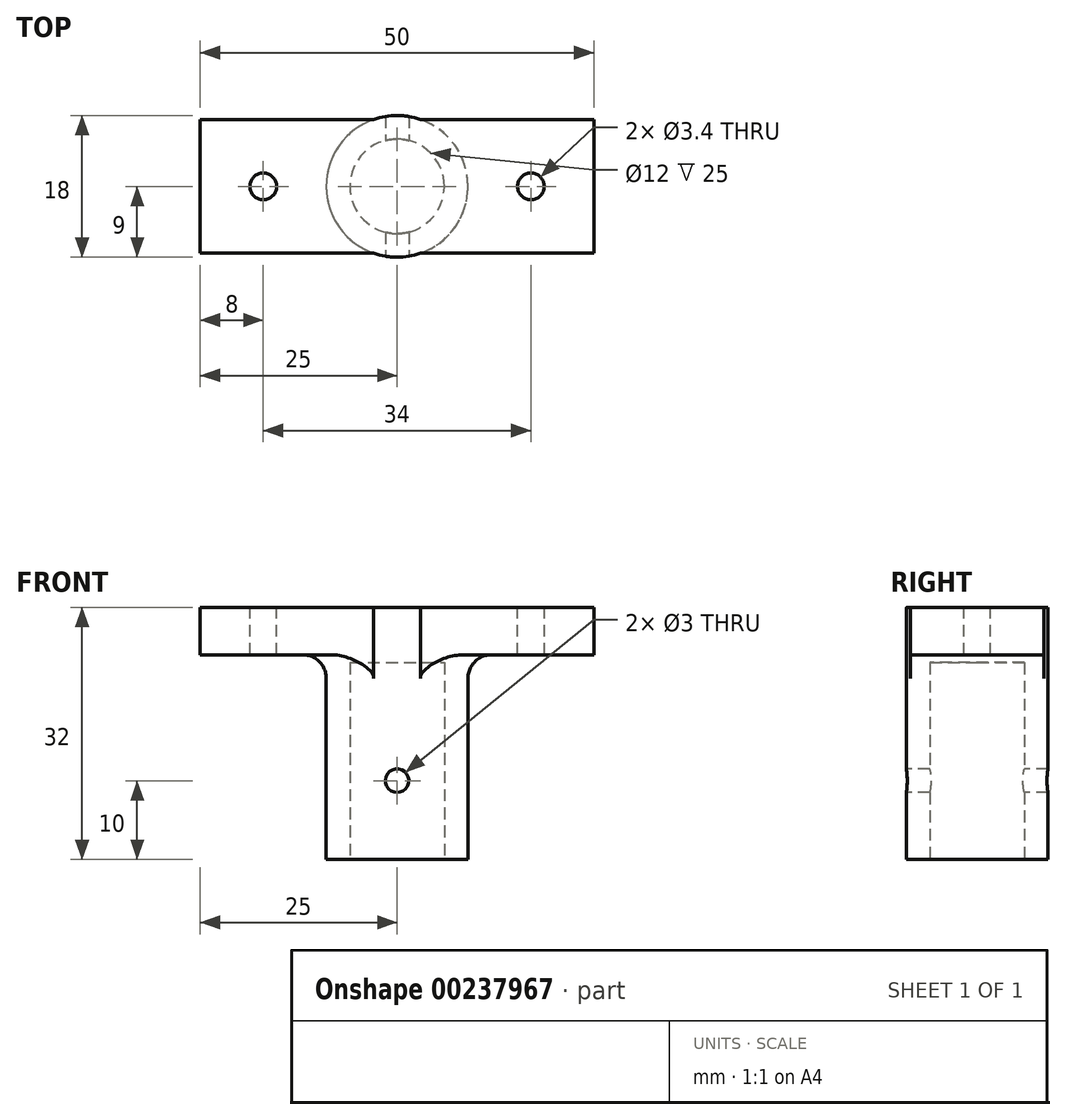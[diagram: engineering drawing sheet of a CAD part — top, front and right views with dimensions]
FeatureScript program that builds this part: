
annotation { "Feature Type Name" : "Feature", "Feature Type Description" : "" }
export const myFeature = defineFeature(function(context is Context, id is Id, definition is map)
    precondition{}
    {
        {
            var Q0;
            Q0=qCreatedBy(makeId("Top.planeOp"),FACE);
            cPlane(context, id + "F0", {"entities" : qUnion([Q0]), "cplaneType" : CPlaneType.OFFSET, "offset" : 70 * mm, "width" : 150 * mm, "height" : 150 * mm});
        }
        {
            var Q0;
            Q0=qCreatedBy(id+"F0.planeOp",FACE);
            var sketch = newSketch(context, id + "F1", { "sketchPlane" : qUnion([Q0])});
            skLineSegment(sketch, "E0.bottom", {"start": v(-25, 8.5) * mm, "end": v(25, 8.5) * mm});
            skLineSegment(sketch, "E0.top", {"start": v(-25, -8.5) * mm, "end": v(25, -8.5) * mm});
            skLineSegment(sketch, "E0.left", {"start": v(-25, 8.5) * mm, "end": v(-25, -8.5) * mm});
            skLineSegment(sketch, "E0.right", {"start": v(25, 8.5) * mm, "end": v(25, -8.5) * mm});
            skCircle(sketch, "E1", {"center": v(-17, 0) * mm, "radius": 1.7 * mm});
            skCircle(sketch, "E2", {"center": v(17, 0) * mm, "radius": 1.7 * mm});
            skSolve(sketch);
        }
        {
            var Q0;
            Q0=makeQuery(id+"F1.imprint","IMPRINT",FACE,{"disambiguationData":[TD([[makeQuery(id+"F1.imprint","IMPRINT",EDGE,{"derivedFrom":sQuery(id+"F1.wireOp",EDGE,"E0.bottom")}),-1.0]])]});
            extrude(context, id + "F2", {"entities" : qUnion([Q0]), "oppositeDirection" : true, "depth" : 6 * mm});
        }
        {
            var Q0;
            Q0=makeQuery(id+"F2.opExtrude","CAP_FACE",FACE,{"disambiguationData":[OSD([sQuery(id+"F1.wireOp",EDGE,"E0.bottom"),sQuery(id+"F1.wireOp",EDGE,"E0.top"),sQuery(id+"F1.wireOp",EDGE,"E0.left"),sQuery(id+"F1.wireOp",EDGE,"E0.right"),sQuery(id+"F1.wireOp",EDGE,"E1"),sQuery(id+"F1.wireOp",EDGE,"E2")])],"isStart":true});
            var sketch = newSketch(context, id + "F3", { "sketchPlane" : qUnion([Q0])});
            skCircle(sketch, "E3", {"center": v(0, 0) * mm, "radius": 9 * mm});
            skSolve(sketch);
        }
        {
            var Q0;
            {var subQ0=sQuery(id+"F3.wireOp",EDGE,"E3");var subQ1=makeQuery(id+"F2.opExtrude","CAP_EDGE",EDGE,{"disambiguationData":[OSD([sQuery(id+"F1.wireOp",EDGE,"E0.bottom")])],"isStart":true});var subQ2=makeQuery(id+"F3.imprint","INTERSECT",VERTEX,{"disambiguationData":[OD(0.0)],"derivedFrom":[subQ1,subQ0]});Q0=makeQuery(id+"F3.imprint","IMPRINT",FACE,{"disambiguationData":[TD([[makeQuery(id+"F3.imprint","IMPRINT",EDGE,{"disambiguationData":[TD([[subQ2,-1.0]])],"derivedFrom":subQ0}),1.0]])]});}
            var Q1;
            {var subQ0=sQuery(id+"F3.wireOp",EDGE,"E3");var subQ1=makeQuery(id+"F2.opExtrude","CAP_EDGE",EDGE,{"disambiguationData":[OSD([sQuery(id+"F1.wireOp",EDGE,"E0.top")])],"isStart":true});var subQ2=makeQuery(id+"F3.imprint","INTERSECT",VERTEX,{"disambiguationData":[OD(0.0)],"derivedFrom":[subQ1,subQ0]});Q1=makeQuery(id+"F3.imprint","IMPRINT",FACE,{"disambiguationData":[TD([[makeQuery(id+"F3.imprint","IMPRINT",EDGE,{"disambiguationData":[TD([[subQ2,-1.0]])],"derivedFrom":subQ0}),1.0]])]});}
            var Q2;
            {var subQ0=sQuery(id+"F3.wireOp",EDGE,"E3");var subQ1=makeQuery(id+"F2.opExtrude","CAP_EDGE",EDGE,{"disambiguationData":[OSD([sQuery(id+"F1.wireOp",EDGE,"E0.bottom")])],"isStart":true});var subQ2=makeQuery(id+"F3.imprint","INTERSECT",VERTEX,{"disambiguationData":[OD(0.0)],"derivedFrom":[subQ1,subQ0]});Q2=makeQuery(id+"F3.imprint","IMPRINT",FACE,{"disambiguationData":[TD([[makeQuery(id+"F3.imprint","IMPRINT",EDGE,{"disambiguationData":[TD([[subQ2,1.0]])],"derivedFrom":subQ0}),1.0]])]});}
            extrude(context, id + "F4", {"entities" : qUnion([Q0, Q1, Q2]), "operationType" : NewBodyOperationType.ADD, "oppositeDirection" : true, "depth" : 32 * mm});
        }
        {
            var Q0;
            Q0=makeQuery(id+"F4.boolean.opBoolean","INTERSECT",EDGE,{"disambiguationData":[OD(0.0)],"derivedFrom":[makeQuery(id+"F2.opExtrude","CAP_FACE",FACE,{"disambiguationData":[OSD([sQuery(id+"F1.wireOp",EDGE,"E0.bottom"),sQuery(id+"F1.wireOp",EDGE,"E0.top"),sQuery(id+"F1.wireOp",EDGE,"E0.left"),sQuery(id+"F1.wireOp",EDGE,"E0.right"),sQuery(id+"F1.wireOp",EDGE,"E1"),sQuery(id+"F1.wireOp",EDGE,"E2")])],"isStart":false}),makeQuery(id+"F4.opExtrude","SWEPT_FACE",FACE,{"disambiguationData":[OSD([sQuery(id+"F3.wireOp",EDGE,"E3")])]})]});
            var Q1;
            Q1=makeQuery(id+"F4.boolean.opBoolean","INTERSECT",EDGE,{"disambiguationData":[OD(1.0)],"derivedFrom":[makeQuery(id+"F2.opExtrude","CAP_FACE",FACE,{"disambiguationData":[OSD([sQuery(id+"F1.wireOp",EDGE,"E0.bottom"),sQuery(id+"F1.wireOp",EDGE,"E0.top"),sQuery(id+"F1.wireOp",EDGE,"E0.left"),sQuery(id+"F1.wireOp",EDGE,"E0.right"),sQuery(id+"F1.wireOp",EDGE,"E1"),sQuery(id+"F1.wireOp",EDGE,"E2")])],"isStart":false}),makeQuery(id+"F4.opExtrude","SWEPT_FACE",FACE,{"disambiguationData":[OSD([sQuery(id+"F3.wireOp",EDGE,"E3")])]})]});
            fillet(context, id + "F5", {"entities" : qUnion([Q0, Q1]), "radius" : 3 * mm, "tangentPropagation" : true, "allowEdgeOverflow" : false});
        }
        {
            var Q0;
            Q0=makeQuery(id+"F4.opExtrude","CAP_FACE",FACE,{"disambiguationData":[OSD([sQuery(id+"F3.wireOp",EDGE,"E3")])],"isStart":false});
            var sketch = newSketch(context, id + "F6", { "sketchPlane" : qUnion([Q0])});
            skCircle(sketch, "E4", {"center": v(0, 0) * mm, "radius": 6 * mm});
            skSolve(sketch);
        }
        {
            var Q0;
            Q0=makeQuery(id+"F6.imprint","IMPRINT",FACE,{"disambiguationData":[TD([[makeQuery(id+"F6.imprint","IMPRINT",EDGE,{"derivedFrom":sQuery(id+"F6.wireOp",EDGE,"E4")}),1.0]])]});
            extrude(context, id + "F7", {"entities" : qUnion([Q0]), "operationType" : NewBodyOperationType.REMOVE, "oppositeDirection" : true, "depth" : 25 * mm});
        }
        {
            var Q0;
            Q0=qCreatedBy(makeId("Front.planeOp"),FACE);
            var sketch = newSketch(context, id + "F8", { "sketchPlane" : qUnion([Q0])});
            skCircle(sketch, "E5", {"center": v(0, 48) * mm, "radius": 1.5 * mm});
            skSolve(sketch);
        }
        {
            var Q0;
            Q0=makeQuery(id+"F8.imprint","IMPRINT",FACE,{"disambiguationData":[TD([[makeQuery(id+"F8.imprint","IMPRINT",EDGE,{"derivedFrom":sQuery(id+"F8.wireOp",EDGE,"E5")}),1.0]])]});
            extrude(context, id + "F9", {"entities" : qUnion([Q0]), "operationType" : NewBodyOperationType.REMOVE, "endBound" : BoundingType.SYMMETRIC, "oppositeDirection" : true, "depth" : 30.4 * mm});
        }
    });
